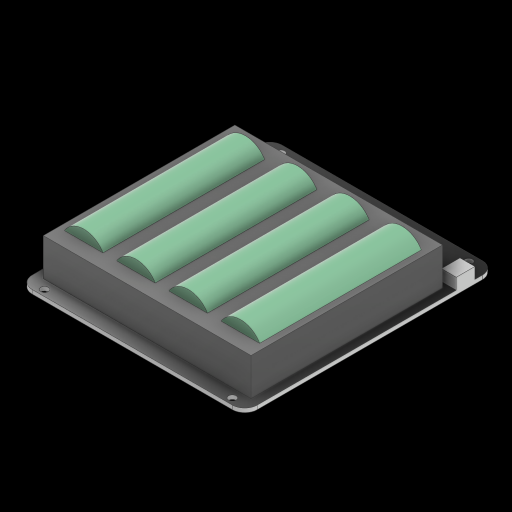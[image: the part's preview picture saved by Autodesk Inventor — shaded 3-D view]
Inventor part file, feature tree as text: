
AUTODESK INVENTOR PART (.ipt)
format: ipt  version: 2024 (Build 280153000, 153)  size: 300,544 bytes
history: native  units: mm
features: sketch x8, extrude x7, fillet x3, plane x1, hole x1
ambient origin geometry x8: Origin, YZ Plane, XZ Plane, XY Plane, X Axis, Y Axis, Z Axis, Center Point
bodies: Volumenkörper1 (feature_tree)
feature tree (20):
  extrude  "Extrusion1"  Depth=100.5mm
  fillet  "Rundung1"  Radius=1.6mm
  extrude  "Extrusion2"  Depth=32.5mm
  fillet  "Rundung2"  Radius=39.5mm
  extrude  "Extrusion3"  Depth=6.5mm
  fillet  "Rundung3"  Radius=5.0mm
  extrude  "Extrusion4"  Depth=7.5mm
  extrude  "Extrusion5"  Depth=9.0mm
  extrude  "Extrusion6"  Depth=2.0mm
  plane  "Arbeitsebene1"
  extrude  "Extrusion7"  Depth=7.5mm
  hole  "Bohrung1"  [1 undecoded]
  sketch  "Skizze1"  dims[d0=90.5mm d1=100.5mm d2=1.6mm d3=0.0mm]
  sketch  "Skizze2"  dims[d4=5.0mm d5=32.5mm d6=39.5mm]
  sketch  "Skizze3"  dims[d7=6.5mm d8=6.5mm d9=5.0mm d10=0.0mm]
  sketch  "Skizze4"  dims[d11=0.5mm d12=7.5mm]
  sketch  "Skizze5"  dims[d13=7.0mm d14=9.0mm]
  sketch  "Skizze6"  dims[d15=5.0mm d16=0.0mm d17=2.0mm]
  sketch  "Skizze7"  dims[d19=8.0mm d20=7.5mm]
  sketch  "Skizze8"  dims[d21=6.0mm d22=8.0mm d23=9.0mm d24=4.5mm d25=2.0mm d26=4.5mm d27=0.0mm d28=1.5mm d29=6.0mm d30=1.0mm d31=2.0mm d32=3.0mm d33=0.0mm d34=6.0mm d35=3.5mm d36=3.5mm d37=77.0mm d38=15.0mm d39=0.0mm d40=-6.0mm d41=18.0mm d42=18.0mm d43=18.0mm d44=18.0mm d45=21.0mm d46=21.0mm d47=21.0mm d49=31.5mm d50=21.0mm d51=65.0mm d52=0.0mm d53=95.0mm d54=75.5mm d55=0.0mm d56=3.0mm d57=3.0mm d58=6.0mm d59=4.0mm d60=2.0mm d61=90.0deg d62=8.0mm d63=20.594885mm]
note: 1 required parameter value undecoded (feature->parameter linkage not recoverable at this tier; creation-order binding heuristic only, values carry confidence <= 0.55)
